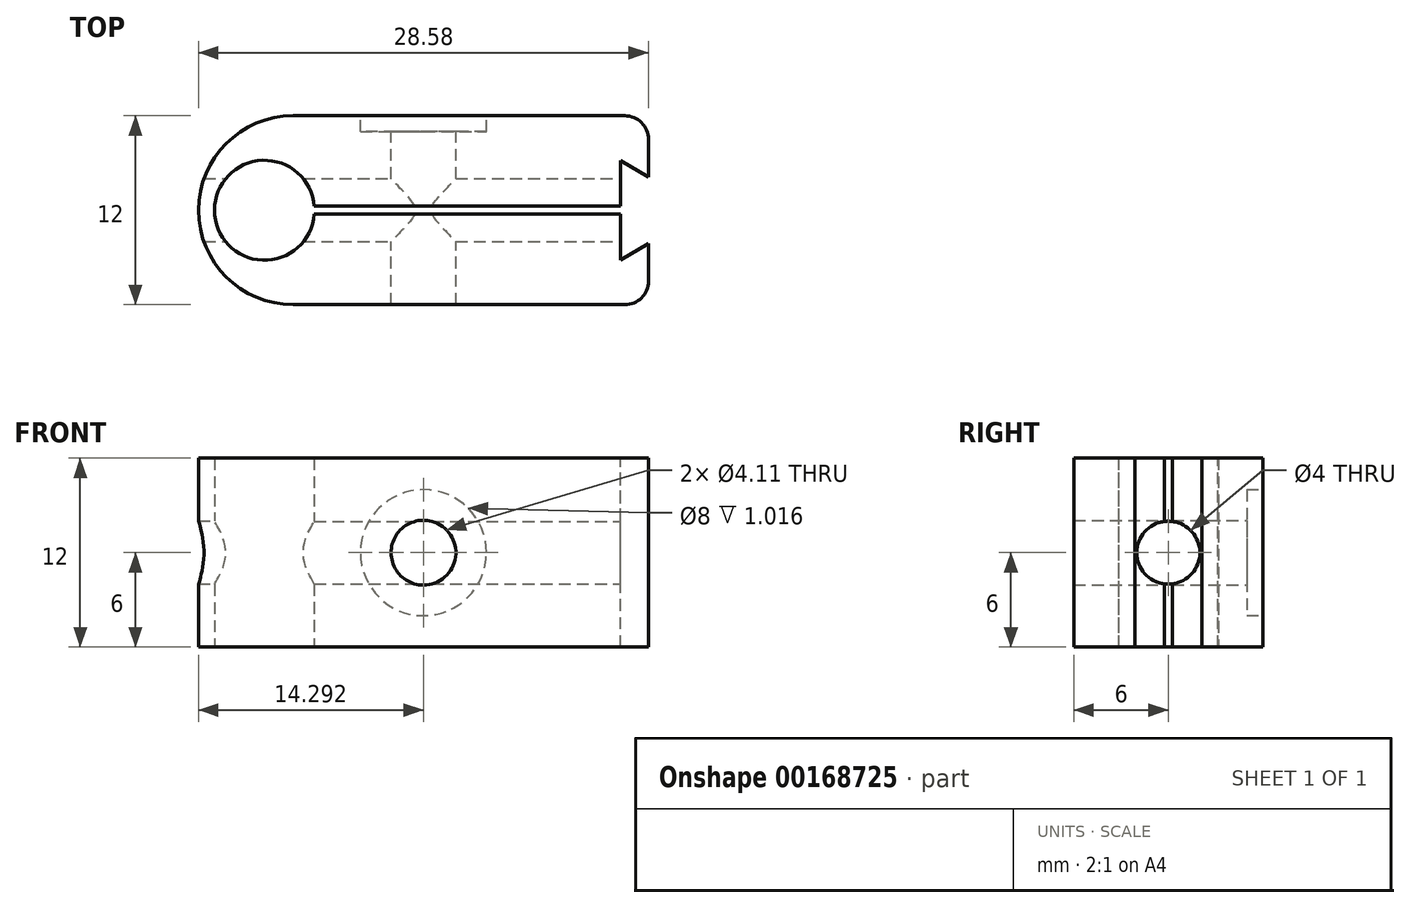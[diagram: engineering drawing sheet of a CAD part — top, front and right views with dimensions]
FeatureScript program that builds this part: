
annotation { "Feature Type Name" : "Feature", "Feature Type Description" : "" }
export const myFeature = defineFeature(function(context is Context, id is Id, definition is map)
    precondition{}
    {
        {
            var Q0;
            Q0=qCreatedBy(makeId("Top.planeOp"),FACE);
            var sketch = newSketch(context, id + "F0", { "sketchPlane" : qUnion([Q0])});
            skLineSegment(sketch, "E0.bottom", {"start": v(-1.5, 0) * mm, "end": v(-22.58, 0) * mm});
            skLineSegment(sketch, "E0.top", {"start": v(-1.5, 12) * mm, "end": v(-22.58, 12) * mm});
            skLineSegment(sketch, "E0.left", {"start": v(0, 1.5) * mm, "end": v(0, 5.75) * mm});
            skArc(sketch, "E1", {"start": v(-22.58, 12) * mm, "mid": v(-28.58, 6) * mm, "end": v(-22.58, 0) * mm});
            skLineSegment(sketch, "E2", {"start": v(-21.22, 6.25) * mm, "end": v(0, 6.25) * mm});
            skLineSegment(sketch, "E3", {"start": v(-21.22, 5.75) * mm, "end": v(0, 5.75) * mm});
            skLineSegment(sketch, "E4", {"start": v(0, 6.25) * mm, "end": v(0, 10.5) * mm});
            skLineSegment(sketch, "E5", {"start": v(-21.22, 6.25) * mm, "end": v(-21.22, 5.75) * mm, "construction": true});
            skPoint(sketch, "E6.visualSharp", {"position": v(0, 12) * mm});
            skArc(sketch, "E6.filletArc", {"start": v(0, 10.5) * mm, "mid": v(-0.44, 11.56) * mm, "end": v(-1.5, 12) * mm});
            skPoint(sketch, "E7.visualSharp", {"position": v(0, 0) * mm});
            skArc(sketch, "E7.filletArc", {"start": v(-1.5, 0) * mm, "mid": v(-0.44, 0.44) * mm, "end": v(0, 1.5) * mm});
            skArc(sketch, "E8", {"start": v(-21.22, 6.25) * mm, "mid": v(-27.56, 6) * mm, "end": v(-21.22, 5.75) * mm});
            skPoint(sketch, "E9", {"position": v(-27.56, 6) * mm});
            skPoint(sketch, "E10", {"position": v(-28.58, 6) * mm});
            skLineSegment(sketch, "E11", {"start": v(-24.38, 2.82) * mm, "end": v(-24.38, 9.17) * mm, "construction": true});
            skSolve(sketch);
        }
        {
            var Q0;
            Q0 = qSketchRegion(id + "F0", true);
            extrude(context, id + "F1", {"entities" : qUnion([Q0]), "depth" : 12 * mm});
        }
        {
            var Q0;
            Q0=makeQuery(id+"F1.opExtrude","SWEPT_FACE",FACE,{"disambiguationData":[OSD([sQuery(id+"F0.wireOp",EDGE,"E0.top")])]});
            var sketch = newSketch(context, id + "F2", { "sketchPlane" : qUnion([Q0])});
            skCircle(sketch, "E12", {"center": v(14.29, 6) * mm, "radius": 2.06 * mm});
            skLineSegment(sketch, "E13", {"start": v(14.29, 6) * mm, "end": v(0, 6) * mm, "construction": true});
            skLineSegment(sketch, "E14", {"start": v(14.29, 6) * mm, "end": v(14.29, 12) * mm, "construction": true});
            skLineSegment(sketch, "E15", {"start": v(14.29, 12) * mm, "end": v(14, 12.12) * mm, "construction": true});
            skLineSegment(sketch, "E16", {"start": v(14.29, 6) * mm, "end": v(14.29, 0) * mm, "construction": true});
            skPoint(sketch, "E17.0", {"position": v(28.58, 12) * mm});
            skPoint(sketch, "E18.0", {"position": v(28.58, 0) * mm});
            skLineSegment(sketch, "E19", {"start": v(28.58, 12) * mm, "end": v(28.58, 0) * mm, "construction": true});
            skLineSegment(sketch, "E20", {"start": v(28.58, 6) * mm, "end": v(14.29, 6) * mm, "construction": true});
            skSolve(sketch);
        }
        {
            var Q0;
            Q0 = qSketchRegion(id + "F2", true);
            extrude(context, id + "F3", {"entities" : qUnion([Q0]), "operationType" : NewBodyOperationType.REMOVE, "endBound" : BoundingType.THROUGH_ALL, "oppositeDirection" : true, "depth" : 25.4 * mm});
        }
        {
            var Q0;
            Q0=makeQuery(id+"F1.opExtrude","SWEPT_FACE",FACE,{"disambiguationData":[OSD([sQuery(id+"F0.wireOp",EDGE,"E0.top")])]});
            var sketch = newSketch(context, id + "F4", { "sketchPlane" : qUnion([Q0])});
            skCircle(sketch, "E21", {"center": v(14.29, 6) * mm, "radius": 4 * mm});
            skSolve(sketch);
        }
        {
            var Q0;
            Q0 = qSketchRegion(id + "F4", true);
            extrude(context, id + "F5", {"entities" : qUnion([Q0]), "operationType" : NewBodyOperationType.REMOVE, "oppositeDirection" : true, "depth" : 1.02 * mm});
        }
        {
            var Q0;
            Q0=makeQuery(id+"F1.opExtrude","SWEPT_FACE",FACE,{"disambiguationData":[OSD([sQuery(id+"F0.wireOp",EDGE,"E0.left")])]});
            var sketch = newSketch(context, id + "F6", { "sketchPlane" : qUnion([Q0])});
            skCircle(sketch, "E22", {"center": v(6, 6) * mm, "radius": 2 * mm});
            skLineSegment(sketch, "E23", {"start": v(6, 6) * mm, "end": v(5.75, 12) * mm, "construction": true});
            skLineSegment(sketch, "E24", {"start": v(6, 6) * mm, "end": v(5.75, 0) * mm, "construction": true});
            skLineSegment(sketch, "E25", {"start": v(6, 6) * mm, "end": v(5.75, 6) * mm, "construction": true});
            skLineSegment(sketch, "E26", {"start": v(6, 6) * mm, "end": v(6.25, 6) * mm, "construction": true});
            skSolve(sketch);
        }
        {
            var Q0;
            Q0 = qSketchRegion(id + "F6", true);
            extrude(context, id + "F7", {"entities" : qUnion([Q0]), "operationType" : NewBodyOperationType.REMOVE, "endBound" : BoundingType.THROUGH_ALL, "oppositeDirection" : true, "depth" : 25.4 * mm});
        }
        {
            var Q0;
            Q0=makeQuery(id+"F1.opExtrude","CAP_FACE",FACE,{"disambiguationData":[OSD([sQuery(id+"F0.wireOp",EDGE,"E0.bottom"),sQuery(id+"F0.wireOp",EDGE,"E0.top"),sQuery(id+"F0.wireOp",EDGE,"E0.left"),sQuery(id+"F0.wireOp",EDGE,"E1"),sQuery(id+"F0.wireOp",EDGE,"E2"),sQuery(id+"F0.wireOp",EDGE,"E3"),sQuery(id+"F0.wireOp",EDGE,"E4"),sQuery(id+"F0.wireOp",EDGE,"66957fd7-fe80-422b-9957-3e01f1d7c0541"),sQuery(id+"F0.wireOp",EDGE,"E6.filletArc"),sQuery(id+"F0.wireOp",EDGE,"E7.filletArc")])],"isStart":false});
            var sketch = newSketch(context, id + "F8", { "sketchPlane" : qUnion([Q0])});
            skLineSegment(sketch, "E27", {"start": v(0, 8.12) * mm, "end": v(-1.78, 9.15) * mm});
            skLineSegment(sketch, "E28", {"start": v(-1.78, 9.15) * mm, "end": v(-1.78, 2.85) * mm});
            skLineSegment(sketch, "E29", {"start": v(-1.78, 2.85) * mm, "end": v(0, 3.88) * mm});
            skLineSegment(sketch, "E30", {"start": v(0, 8.12) * mm, "end": v(0, 6.25) * mm});
            skLineSegment(sketch, "E31", {"start": v(0, 6.25) * mm, "end": v(0, 5.75) * mm});
            skLineSegment(sketch, "E32", {"start": v(0, 5.75) * mm, "end": v(0, 3.88) * mm});
            skSolve(sketch);
        }
        {
            var Q0;
            Q0 = qSketchRegion(id + "F8", true);
            extrude(context, id + "F9", {"entities" : qUnion([Q0]), "operationType" : NewBodyOperationType.REMOVE, "endBound" : BoundingType.THROUGH_ALL, "oppositeDirection" : true, "depth" : 25.4 * mm});
        }
    });
